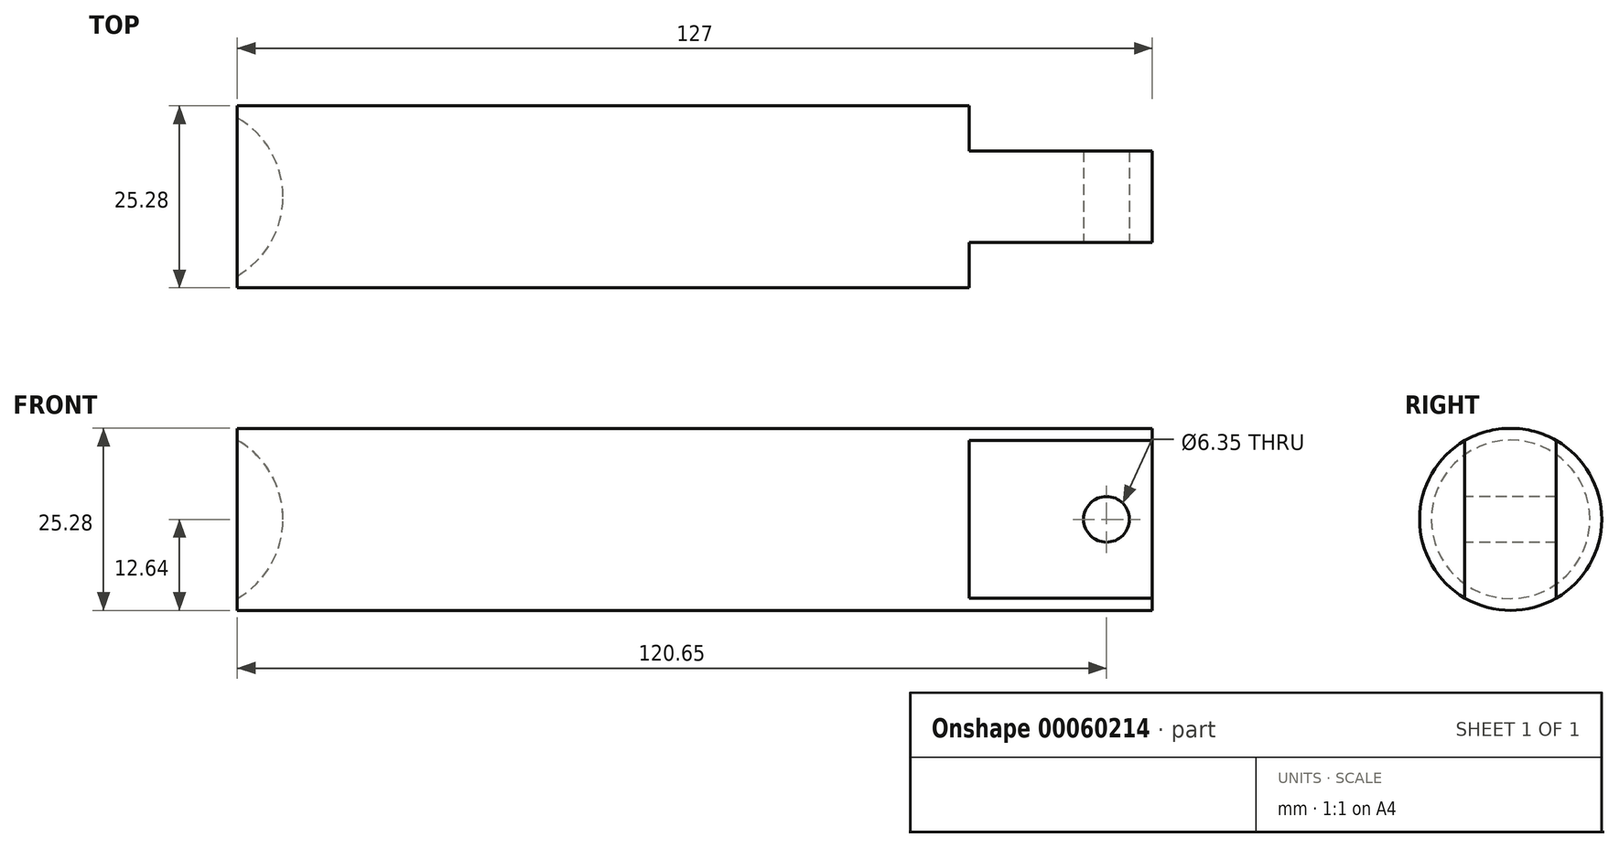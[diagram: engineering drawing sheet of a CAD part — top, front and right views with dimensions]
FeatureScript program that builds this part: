
annotation { "Feature Type Name" : "Feature", "Feature Type Description" : "" }
export const myFeature = defineFeature(function(context is Context, id is Id, definition is map)
    precondition{}
    {
        {
            var Q0;
            Q0=qCreatedBy(makeId("Front.planeOp"),FACE);
            var sketch = newSketch(context, id + "F0", { "sketchPlane" : qUnion([Q0])});
            skLineSegment(sketch, "E0", {"start": v(6.35, 12.64) * mm, "end": v(6.35, 11) * mm});
            skLineSegment(sketch, "E1", {"start": v(12.7, 0) * mm, "end": v(133.35, 0) * mm});
            skLineSegment(sketch, "E2", {"start": v(133.35, 0) * mm, "end": v(133.35, 12.64) * mm});
            skLineSegment(sketch, "E3", {"start": v(133.35, 12.64) * mm, "end": v(6.35, 12.64) * mm});
            skArc(sketch, "E4", {"start": v(12.7, 0) * mm, "mid": v(11, 6.35) * mm, "end": v(6.35, 11) * mm});
            skSolve(sketch);
        }
        {
            var Q0;
            Q0 = qSketchRegion(id + "F0", true);
            var Q1;
            Q1=sQuery(id+"F0.wireOp",EDGE,"E1");
            revolve(context, id + "F1", {"entities" : qUnion([Q0]), "axis" : qUnion([Q1]), "revolveType" : RevolveType.FULL});
        }
        {
            var Q0;
            Q0=qCreatedBy(makeId("Top.planeOp"),FACE);
            var sketch = newSketch(context, id + "F2", { "sketchPlane" : qUnion([Q0])});
            skLineSegment(sketch, "E5.bottom", {"start": v(107.95, 12.64) * mm, "end": v(133.35, 12.64) * mm});
            skLineSegment(sketch, "E5.top", {"start": v(107.95, 6.35) * mm, "end": v(133.35, 6.35) * mm});
            skLineSegment(sketch, "E5.left", {"start": v(107.95, 12.64) * mm, "end": v(107.95, 6.35) * mm});
            skLineSegment(sketch, "E5.right", {"start": v(133.35, 12.64) * mm, "end": v(133.35, 6.35) * mm});
            skLineSegment(sketch, "E6.bottom", {"start": v(107.95, -6.35) * mm, "end": v(133.35, -6.35) * mm});
            skLineSegment(sketch, "E6.top", {"start": v(107.95, -12.65) * mm, "end": v(133.35, -12.65) * mm});
            skLineSegment(sketch, "E6.left", {"start": v(107.95, -6.35) * mm, "end": v(107.95, -12.65) * mm});
            skLineSegment(sketch, "E6.right", {"start": v(133.35, -6.35) * mm, "end": v(133.35, -12.65) * mm});
            skSolve(sketch);
        }
        {
            var Q0;
            Q0 = qSketchRegion(id + "F2", true);
            extrude(context, id + "F3", {"entities" : qUnion([Q0]), "operationType" : NewBodyOperationType.REMOVE, "oppositeDirection" : true, "depth" : 127 * mm, "symmetric" : true});
        }
        {
            var Q0;
            Q0=makeQuery(id+"F3.boolean.opBoolean","COPY",FACE,{"derivedFrom":makeQuery(id+"F3.opExtrude","SWEPT_FACE",FACE,{"disambiguationData":[OSD([sQuery(id+"F2.wireOp",EDGE,"E6.bottom")])]})});
            var sketch = newSketch(context, id + "F4", { "sketchPlane" : qUnion([Q0])});
            skCircle(sketch, "E7", {"center": v(127, 0) * mm, "radius": 3.18 * mm});
            skSolve(sketch);
        }
        {
            var Q0;
            Q0 = qSketchRegion(id + "F4", true);
            extrude(context, id + "F5", {"entities" : qUnion([Q0]), "operationType" : NewBodyOperationType.REMOVE, "oppositeDirection" : true, "depth" : 50.8 * mm});
        }
    });
